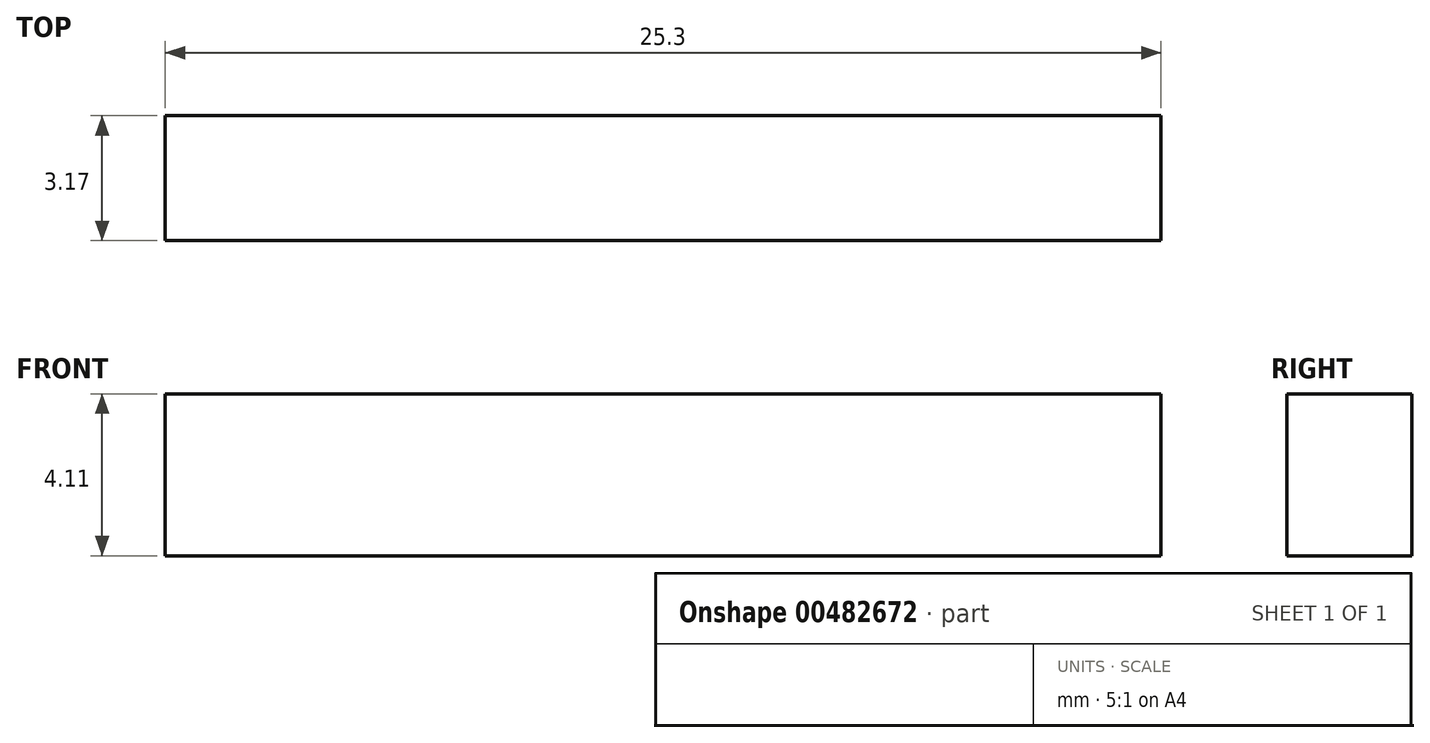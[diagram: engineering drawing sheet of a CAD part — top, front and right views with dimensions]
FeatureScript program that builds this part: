
annotation { "Feature Type Name" : "Feature", "Feature Type Description" : "" }
export const myFeature = defineFeature(function(context is Context, id is Id, definition is map)
    precondition{}
    {
        {
            var Q0;
            Q0=qCreatedBy(makeId("Front.planeOp"),FACE);
            var sketch = newSketch(context, id + "F0", { "sketchPlane" : qUnion([Q0])});
            skLineSegment(sketch, "E0.bottom", {"start": v(0, 0) * mm, "end": v(25.3, 0) * mm});
            skLineSegment(sketch, "E0.top", {"start": v(0, 4.11) * mm, "end": v(25.3, 4.11) * mm});
            skLineSegment(sketch, "E0.left", {"start": v(0, 0) * mm, "end": v(0, 4.11) * mm});
            skLineSegment(sketch, "E0.right", {"start": v(25.3, 0) * mm, "end": v(25.3, 4.11) * mm});
            skSolve(sketch);
        }
        {
            var Q0;
            Q0=makeQuery(id+"F0.imprint","IMPRINT",FACE,{"disambiguationData":[TD([[makeQuery(id+"F0.imprint","IMPRINT",EDGE,{"derivedFrom":sQuery(id+"F0.wireOp",EDGE,"E0.bottom")}),1.0]])]});
            extrude(context, id + "F1", {"entities" : qUnion([Q0]), "depth" : 3.17 * mm});
        }
    });
